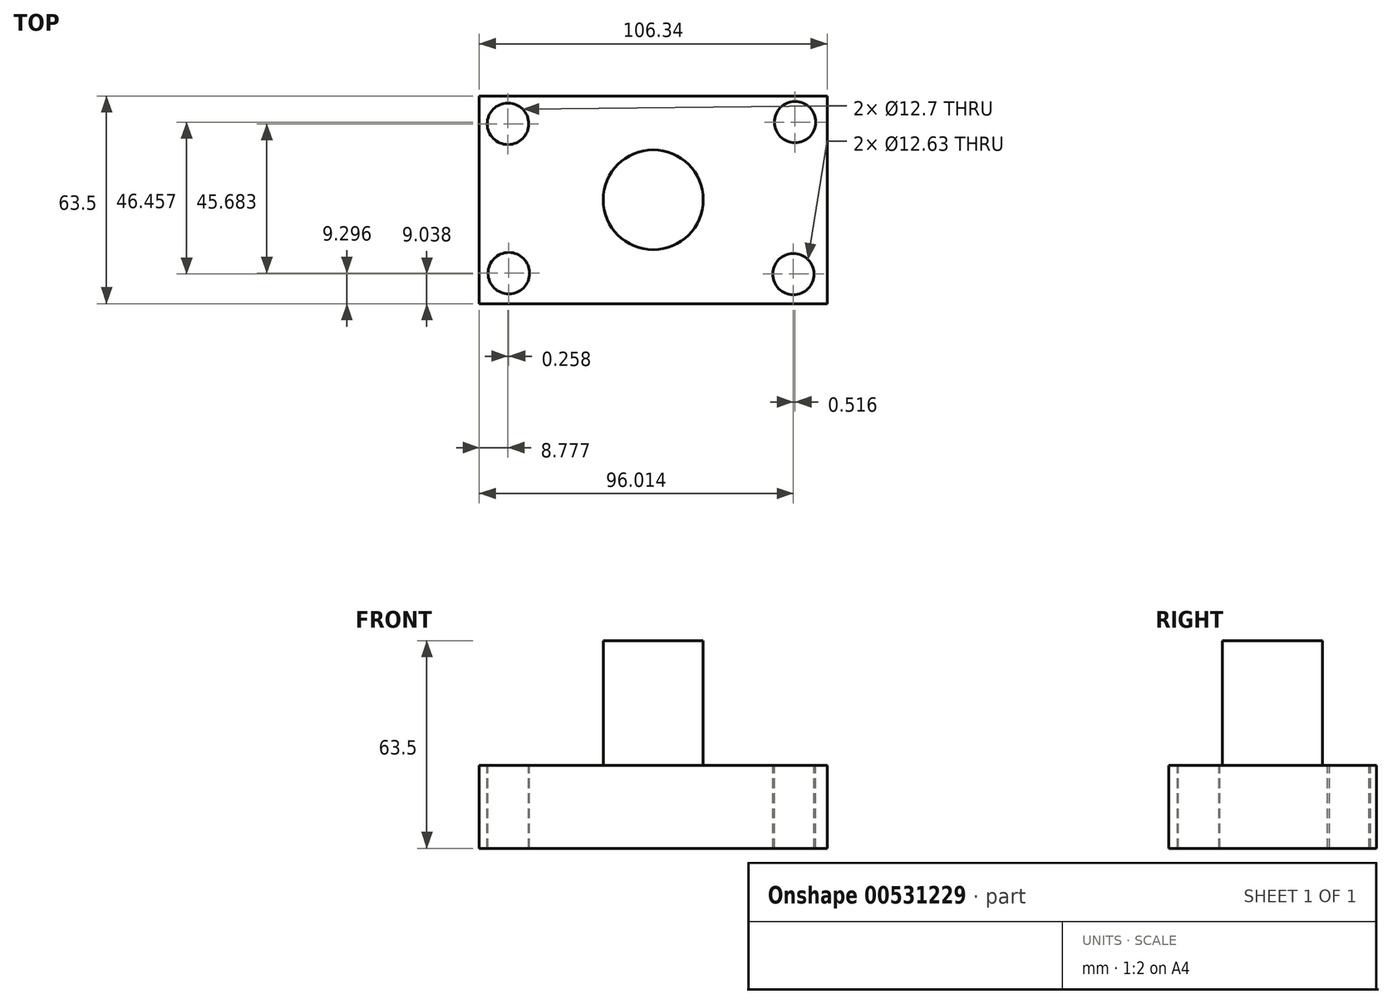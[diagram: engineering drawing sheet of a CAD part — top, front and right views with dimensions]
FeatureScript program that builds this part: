
annotation { "Feature Type Name" : "Feature", "Feature Type Description" : "" }
export const myFeature = defineFeature(function(context is Context, id is Id, definition is map)
    precondition{}
    {
        {
            var Q0;
            Q0=qCreatedBy(makeId("Top.planeOp"),FACE);
            var sketch = newSketch(context, id + "F0", { "sketchPlane" : qUnion([Q0])});
            skLineSegment(sketch, "E0.bottom", {"start": v(53.17, 31.75) * mm, "end": v(-53.17, 31.75) * mm});
            skLineSegment(sketch, "E0.top", {"start": v(53.17, -31.75) * mm, "end": v(-53.17, -31.75) * mm});
            skLineSegment(sketch, "E0.left", {"start": v(53.17, 31.75) * mm, "end": v(53.17, -31.75) * mm});
            skLineSegment(sketch, "E0.right", {"start": v(-53.17, 31.75) * mm, "end": v(-53.17, -31.75) * mm});
            skPoint(sketch, "E0.middle", {"position": v(0, 0) * mm});
            skSolve(sketch);
        }
        {
            var Q0;
            Q0 = qSketchRegion(id + "F0", true);
            extrude(context, id + "F1", {"entities" : qUnion([Q0]), "depth" : 25.4 * mm, "offsetDistance" : 25.4 * mm});
        }
        {
            var Q0;
            Q0=makeQuery(id+"F1.opExtrude","CAP_FACE",FACE,{"disambiguationData":[OSD([sQuery(id+"F0.wireOp",EDGE,"E0.bottom"),sQuery(id+"F0.wireOp",EDGE,"E0.top"),sQuery(id+"F0.wireOp",EDGE,"E0.left"),sQuery(id+"F0.wireOp",EDGE,"E0.right")])],"isStart":false});
            var sketch = newSketch(context, id + "F2", { "sketchPlane" : qUnion([Q0])});
            skCircle(sketch, "E1", {"center": v(-44.4, 23.23) * mm, "radius": 6.35 * mm});
            skCircle(sketch, "E2", {"center": v(-44.13, -22.45) * mm, "radius": 6.35 * mm});
            skCircle(sketch, "E3", {"center": v(43.36, 23.74) * mm, "radius": 6.31 * mm});
            skCircle(sketch, "E4", {"center": v(42.84, -22.71) * mm, "radius": 6.31 * mm});
            skSolve(sketch);
        }
        {
            var Q0;
            Q0=makeQuery(id+"F2.imprint","IMPRINT",FACE,{"disambiguationData":[TD([[makeQuery(id+"F2.imprint","IMPRINT",EDGE,{"derivedFrom":sQuery(id+"F2.wireOp",EDGE,"E1")}),1.0]])]});
            var Q1;
            Q1=makeQuery(id+"F2.imprint","IMPRINT",FACE,{"disambiguationData":[TD([[makeQuery(id+"F2.imprint","IMPRINT",EDGE,{"derivedFrom":sQuery(id+"F2.wireOp",EDGE,"E2")}),1.0]])]});
            var Q2;
            Q2=makeQuery(id+"F2.imprint","IMPRINT",FACE,{"disambiguationData":[TD([[makeQuery(id+"F2.imprint","IMPRINT",EDGE,{"derivedFrom":sQuery(id+"F2.wireOp",EDGE,"E3")}),1.0]])]});
            var Q3;
            Q3=makeQuery(id+"F2.imprint","IMPRINT",FACE,{"disambiguationData":[TD([[makeQuery(id+"F2.imprint","IMPRINT",EDGE,{"derivedFrom":sQuery(id+"F2.wireOp",EDGE,"E4")}),1.0]])]});
            extrude(context, id + "F3", {"entities" : qUnion([Q0, Q1, Q2, Q3]), "operationType" : NewBodyOperationType.REMOVE, "oppositeDirection" : true, "depth" : 25.4 * mm, "offsetDistance" : 25.4 * mm});
        }
        {
            var Q0;
            Q0=makeQuery(id+"F1.opExtrude","CAP_FACE",FACE,{"disambiguationData":[OSD([sQuery(id+"F0.wireOp",EDGE,"E0.bottom"),sQuery(id+"F0.wireOp",EDGE,"E0.top"),sQuery(id+"F0.wireOp",EDGE,"E0.left"),sQuery(id+"F0.wireOp",EDGE,"E0.right")])],"isStart":false});
            var sketch = newSketch(context, id + "F4", { "sketchPlane" : qUnion([Q0])});
            skCircle(sketch, "E5", {"center": v(0, 0) * mm, "radius": 15.28 * mm});
            skSolve(sketch);
        }
        {
            var Q0;
            Q0=makeQuery(id+"F4.imprint","IMPRINT",FACE,{"disambiguationData":[TD([[makeQuery(id+"F4.imprint","IMPRINT",EDGE,{"derivedFrom":sQuery(id+"F4.wireOp",EDGE,"E5")}),1.0]])]});
            extrude(context, id + "F5", {"entities" : qUnion([Q0]), "operationType" : NewBodyOperationType.ADD, "depth" : 38.1 * mm, "offsetDistance" : 25.4 * mm});
        }
    });
